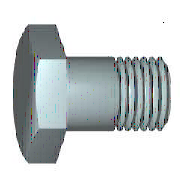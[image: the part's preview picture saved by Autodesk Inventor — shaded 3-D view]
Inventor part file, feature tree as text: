
AUTODESK INVENTOR PART (.ipt)
format: ipt  version: 2022 (Build 260153000, 153)  size: 191,488 bytes
history: native  units: mm (DEFAULTED — no unit token found)
features: sketch x3, extrude x1, chamfer x1, plane x1
ambient origin geometry x7: Origin, YZ Plane, XZ Plane, X Axis, Y Axis, Z Axis, Center Point
bodies: Solid1 (feature_tree), Body (feature_tree)
feature tree (6):
  extrude  "Head"  Depth=22.0mm
  chamfer  "Chamfer1"  Distance=4.7mm
  plane  "Work Plane1"
  sketch  "Sketch1"  dims[d0=60.0mm d1=22.0mm]
  sketch  "Sketch2"  dims[d2=8.0mm]
  sketch  "Sketch4"  dims[d12=90.0deg d3=4.7mm d4=0.0mm d5=30.0deg d21=90.0deg d6=0.766813mm d7=0.766912mm d8=0.0mm d9=0.6001mm d10=11.63mm d11=13.0mm d13=0.766912mm d14=8.0mm d15=22.0mm d16=0.0mm d19=13.0mm d55=45.0deg d57=0.0mm d58=0.0mm]
